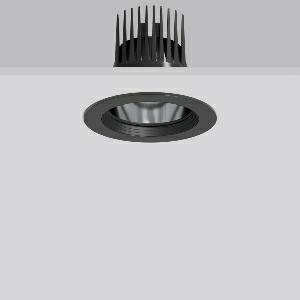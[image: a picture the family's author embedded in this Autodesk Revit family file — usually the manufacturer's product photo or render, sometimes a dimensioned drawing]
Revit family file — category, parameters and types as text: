
# Revit family: heledon_maxi_e_901756_003_3_f949
name_source: partatom
category: Lighting Fixtures
units: mm (PartAtom-declared; Revit-internal decimal feet)

## family parameters
Cut with Voids When Loaded = No
Host = Face
Light Source = No
Part Type = Normal
Room Calculation Point = No
Round Connector Dimension = Use Diameter
Shared = No

## types (1)
- HELEDON maxi E (1 x LED Modul 935, 3300 lm, 3500)
    Apparent Load = 25 VA
    Approval mark = CE
    CIE Flux Codes = 100 100 100 100 100
    Color Rendering = 92
    Color Temperature = 3500
    Default Elevation = 1800 mm
    Description = Series: HELEDON maxi
Round recessed downlight. Housing: die-cast aluminium, powder-coated. Black plastic ring and recessed LED to prevent glare from the side. Optical assembly with reflector made of MIRO-Silver with 98% total light reflection for outstanding efficiency - can be changed without tools. Best colour rendering index Ra>90. Suitable for Recessed ceiling mounting. Installation without tools thanks to spring fastening system. Including separate LED converter with connecting cable 600 mm.High quality converter without flickering and stroboscopic effect. Through-wiring box (5 pole) available as accessory. The following accessories can be mounted without use of tools: interchangeable lenses, decorative glasses, honeycomb louvre, clear and frosted diffusers, white interchangeable plastic ring. 
Colour: deep black, matt (RAL 9005)
Diameter: 162 mm
Height: 3 mm
Cut-out diameter: 152 mm
Recess height: 200 mm
Luminaire: recess height: 135 mm
Lamp: LED
Socket: without socket
Colour temperature: 3500K
Colour rendering index (CRI): 92
System power: 25 W
Rated luminous flux: 3300 lm
Luminous efficiency: 132 lm/W
Control gear: Regulated power supply
Protection class: II
Type of protection: IP 20
    Height = 0 mm  [stored 0 ft]
    Lamp = 1 x LED Modul 935
    Lamp Light Flux = 3300 lm
    Lamp count = 1
    Length = 162 mm
    Lifetime = 50000 h
    Luminous efficacy = 132 lm/W
    Manufacturer = RZB
    ModVariant = No
    Model = 901756.003.3
    Mounting Place = Ceiling
    Mounting Type = Recessed
    Number of Poles = 1
    OnlyDefault = Yes
    Power Factor = 1
    Product Name = HELEDON maxi E
    Product group = Recessed downlights
    ProductGroupID = 402
    Protection Class = Protection class II
    Protection Degree = IP 20
    RLX_Detail_Level = 1
    RLX_Emergency_Light_Flux = 0 lm
    RLX_Emergency_Type = 0
    RLX_Emergency_Type_DB = No
    RlxData = <blob elided: 119485 chars, md5=b8eb57d4>
    Socket = socket
    Standby Power = 0 W
    System Light Flux = 3300 lm
    System Power = 25 W
    Type Comments = Product without accessories
    Type Image = 901662.003.jpg
    URL = http://relux.com
    VarID = ---
    Voltage = 230 V
    Voltage Range = 220-240 V
    Weight = 0.00 kg
    Width = 0 mm  [stored 0 ft]

note: [stored X ft] marks values corroborated as IEEE doubles in the binary element streams (Revit-internal decimal feet)

## geometry (parser evidence)
native form markers: Blend x4, Sweep x10
no freeform markers — native parametric forms only
